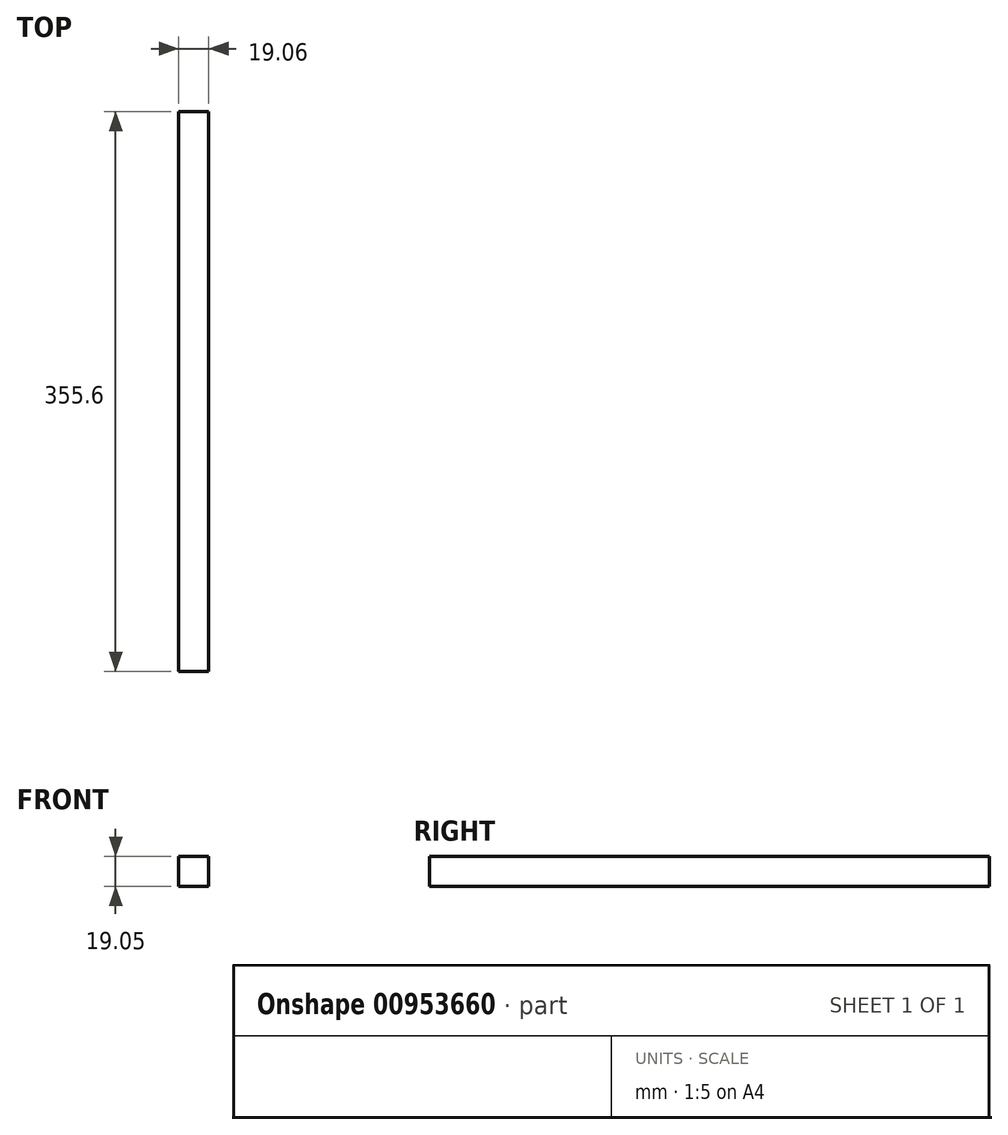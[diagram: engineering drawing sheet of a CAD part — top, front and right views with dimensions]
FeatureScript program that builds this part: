
annotation { "Feature Type Name" : "Feature", "Feature Type Description" : "" }
export const myFeature = defineFeature(function(context is Context, id is Id, definition is map)
    precondition{}
    {
        {
            var Q0;
            Q0=qCreatedBy(makeId("Top.planeOp"),FACE);
            var sketch = newSketch(context, id + "F0", { "sketchPlane" : qUnion([Q0])});
            skLineSegment(sketch, "E0.bottom", {"start": v(9.52, -177.8) * mm, "end": v(-9.53, -177.8) * mm});
            skLineSegment(sketch, "E0.top", {"start": v(9.53, 177.8) * mm, "end": v(-9.52, 177.8) * mm});
            skLineSegment(sketch, "E0.left", {"start": v(9.52, -177.8) * mm, "end": v(9.53, 177.8) * mm});
            skLineSegment(sketch, "E0.right", {"start": v(-9.53, -177.8) * mm, "end": v(-9.52, 177.8) * mm});
            skPoint(sketch, "E0.middle", {"position": v(0, 0) * mm});
            skSolve(sketch);
        }
        {
            var Q0;
            Q0=makeQuery(id+"F0.imprint","IMPRINT",FACE,{"disambiguationData":[TD([[makeQuery(id+"F0.imprint","IMPRINT",EDGE,{"derivedFrom":sQuery(id+"F0.wireOp",EDGE,"E0.bottom")}),-1.0]])]});
            extrude(context, id + "F1", {"entities" : qUnion([Q0]), "depth" : 19.05 * mm, "offsetDistance" : 25.4 * mm});
        }
    });
